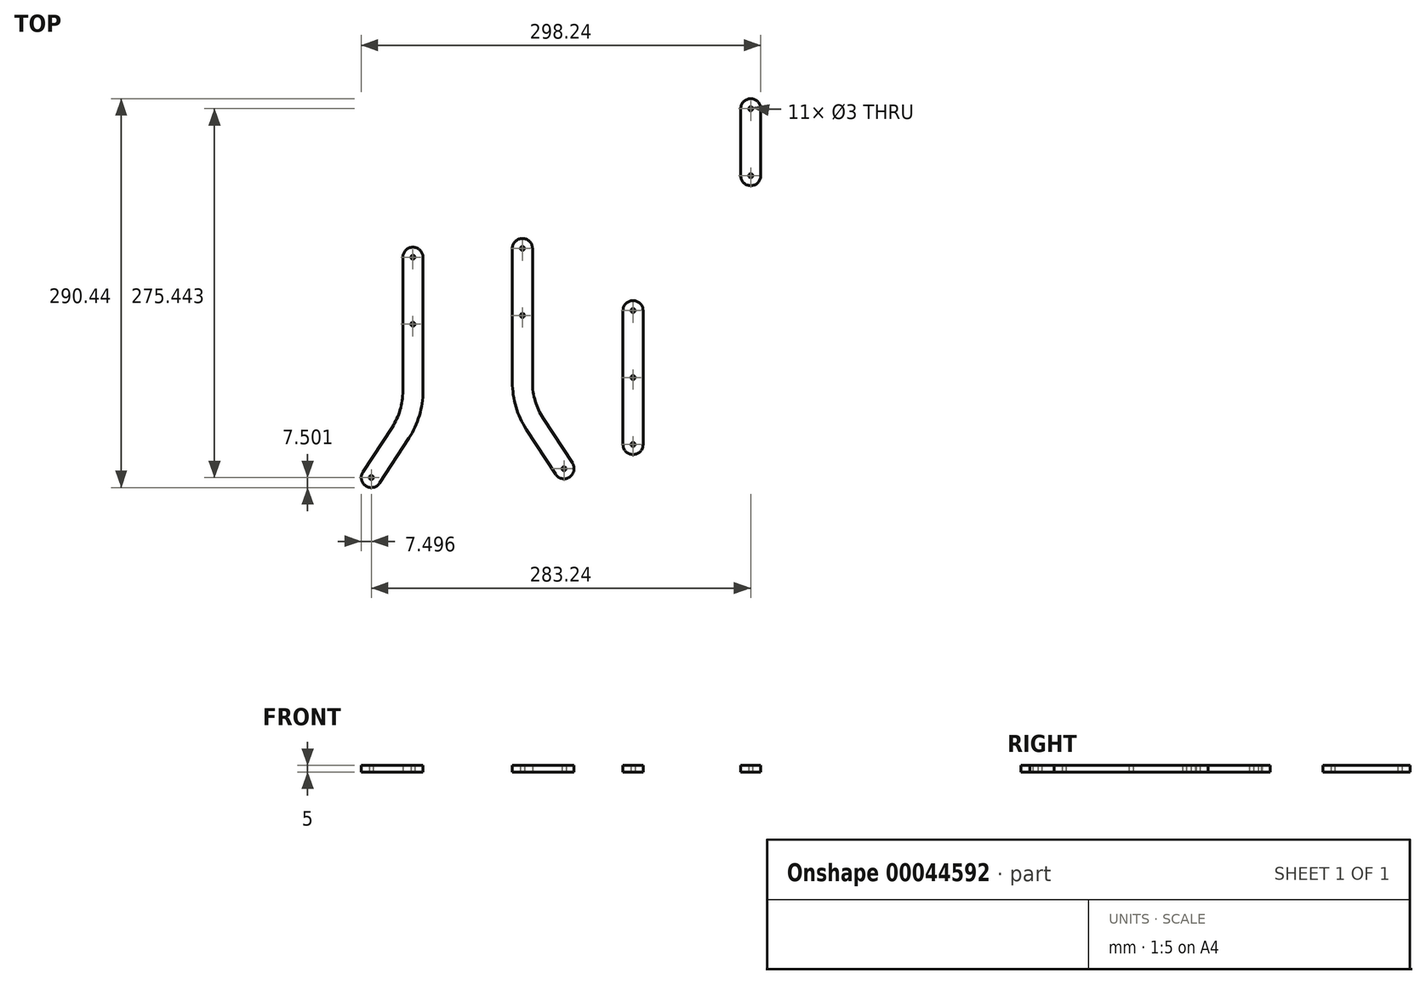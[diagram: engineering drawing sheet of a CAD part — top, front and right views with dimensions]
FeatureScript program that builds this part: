
annotation { "Feature Type Name" : "Feature", "Feature Type Description" : "" }
export const myFeature = defineFeature(function(context is Context, id is Id, definition is map)
    precondition{}
    {
        {
            var Q0;
            Q0=qCreatedBy(makeId("Top.planeOp"),FACE);
            var sketch = newSketch(context, id + "F0", { "sketchPlane" : qUnion([Q0])});
            skLineSegment(sketch, "E0", {"start": v(25.87, 19.2) * mm, "end": v(25.87, -80.8) * mm});
            skArc(sketch, "E1", {"start": v(25.87, -80.8) * mm, "mid": v(33.37, -88.3) * mm, "end": v(40.87, -80.8) * mm});
            skLineSegment(sketch, "E2", {"start": v(25.87, 19.2) * mm, "end": v(40.87, 19.2) * mm});
            skLineSegment(sketch, "E3", {"start": v(25.87, -80.8) * mm, "end": v(40.87, -80.8) * mm});
            skLineSegment(sketch, "E4", {"start": v(40.87, 19.2) * mm, "end": v(40.87, -80.8) * mm});
            skArc(sketch, "E5", {"start": v(40.87, 19.2) * mm, "mid": v(33.37, 26.7) * mm, "end": v(25.87, 19.2) * mm});
            skPoint(sketch, "E6", {"position": v(33.37, -30.8) * mm});
            skCircle(sketch, "E7", {"center": v(33.37, 19.2) * mm, "radius": 1.5 * mm});
            skCircle(sketch, "E8", {"center": v(33.37, -80.8) * mm, "radius": 1.5 * mm});
            skPoint(sketch, "E9", {"position": v(33.37, -5.8) * mm});
            skCircle(sketch, "E10", {"center": v(33.37, -30.8) * mm, "radius": 1.5 * mm});
            skSolve(sketch);
        }
        {
            var Q0;
            {var subQ9=sQuery(id+"F0.wireOp",EDGE,"E0");Q0=makeQuery(id+"F0.imprint","IMPRINT",FACE,{"disambiguationData":[TD([[makeQuery(id+"F0.imprint","IMPRINT",EDGE,{"derivedFrom":subQ9}),1.0]])]});}
            var Q1;
            {var subQ4=sQuery(id+"F0.wireOp",EDGE,"E5");Q1=makeQuery(id+"F0.imprint","IMPRINT",FACE,{"disambiguationData":[TD([[makeQuery(id+"F0.imprint","IMPRINT",EDGE,{"derivedFrom":subQ4}),1.0]])]});}
            var Q2;
            {var subQ4=sQuery(id+"F0.wireOp",EDGE,"E1");Q2=makeQuery(id+"F0.imprint","IMPRINT",FACE,{"disambiguationData":[TD([[makeQuery(id+"F0.imprint","IMPRINT",EDGE,{"derivedFrom":subQ4}),1.0]])]});}
            extrude(context, id + "F1", {"entities" : qUnion([Q0, Q1, Q2]), "depth" : 5 * mm});
        }
        {
            var Q0;
            Q0=qCreatedBy(makeId("Top.planeOp"),FACE);
            var sketch = newSketch(context, id + "F2", { "sketchPlane" : qUnion([Q0])});
            skLineSegment(sketch, "E11", {"start": v(-56.7, 65.62) * mm, "end": v(-56.7, -34.38) * mm});
            skArc(sketch, "E12", {"start": v(-56.7, -34.38) * mm, "mid": v(-54.04, -52.7) * mm, "end": v(-46.27, -69.49) * mm});
            skLineSegment(sketch, "E13", {"start": v(-46.27, -69.49) * mm, "end": v(-24.43, -103) * mm});
            skLineSegment(sketch, "E14", {"start": v(-24.43, -103) * mm, "end": v(-11.86, -94.8) * mm});
            skArc(sketch, "E15", {"start": v(-24.43, -103) * mm, "mid": v(-14.05, -105.19) * mm, "end": v(-11.86, -94.8) * mm});
            skLineSegment(sketch, "E16", {"start": v(-46.27, -69.49) * mm, "end": v(-33.7, -61.3) * mm});
            skLineSegment(sketch, "E17", {"start": v(-33.7, -61.3) * mm, "end": v(-11.86, -94.8) * mm});
            skLineSegment(sketch, "E18", {"start": v(-56.7, 65.62) * mm, "end": v(-41.7, 65.62) * mm});
            skLineSegment(sketch, "E19", {"start": v(-56.7, -34.38) * mm, "end": v(-41.7, -34.38) * mm});
            skLineSegment(sketch, "E20", {"start": v(-41.7, 65.62) * mm, "end": v(-41.7, -34.38) * mm});
            skArc(sketch, "E21", {"start": v(-41.7, -34.38) * mm, "mid": v(-39.66, -48.42) * mm, "end": v(-33.7, -61.3) * mm});
            skArc(sketch, "E22", {"start": v(-41.7, 65.62) * mm, "mid": v(-49.2, 73.12) * mm, "end": v(-56.7, 65.62) * mm});
            skLineSegment(sketch, "E23", {"start": v(-123.46, 59.06) * mm, "end": v(-123.46, -40.94) * mm});
            skLineSegment(sketch, "E24", {"start": v(-123.46, 59.06) * mm, "end": v(-138.46, 59.06) * mm});
            skArc(sketch, "E25", {"start": v(-123.46, 59.06) * mm, "mid": v(-130.96, 66.56) * mm, "end": v(-138.46, 59.06) * mm});
            skLineSegment(sketch, "E26", {"start": v(-138.46, 59.06) * mm, "end": v(-138.46, -40.94) * mm});
            skLineSegment(sketch, "E27", {"start": v(-138.46, -40.94) * mm, "end": v(-123.46, -40.94) * mm});
            skArc(sketch, "E28", {"start": v(-123.46, -40.94) * mm, "mid": v(-126.12, -59.26) * mm, "end": v(-133.9, -76.05) * mm});
            skLineSegment(sketch, "E29", {"start": v(-133.9, -76.05) * mm, "end": v(-155.73, -109.56) * mm});
            skLineSegment(sketch, "E30", {"start": v(-155.73, -109.56) * mm, "end": v(-168.3, -101.37) * mm});
            skLineSegment(sketch, "E31", {"start": v(-133.9, -76.05) * mm, "end": v(-146.46, -67.86) * mm});
            skLineSegment(sketch, "E32", {"start": v(-146.46, -67.86) * mm, "end": v(-168.3, -101.37) * mm});
            skArc(sketch, "E33", {"start": v(-146.46, -67.86) * mm, "mid": v(-140.5, -54.98) * mm, "end": v(-138.46, -40.94) * mm});
            skArc(sketch, "E34", {"start": v(-168.3, -101.37) * mm, "mid": v(-166.1, -111.75) * mm, "end": v(-155.73, -109.56) * mm});
            skPoint(sketch, "E35", {"position": v(-111.62, 71.38) * mm});
            skCircle(sketch, "E36", {"center": v(-130.96, 59.06) * mm, "radius": 1.5 * mm});
            skCircle(sketch, "E37", {"center": v(-162.01, -105.47) * mm, "radius": 1.5 * mm});
            skLineSegment(sketch, "E38", {"start": v(-130.96, 59.06) * mm, "end": v(-130.96, 9.06) * mm});
            skCircle(sketch, "E39", {"center": v(-130.96, 9.06) * mm, "radius": 1.5 * mm});
            skCircle(sketch, "E40", {"center": v(-49.2, 65.62) * mm, "radius": 1.5 * mm});
            skLineSegment(sketch, "E41", {"start": v(-49.2, 65.62) * mm, "end": v(-49.2, 15.62) * mm});
            skCircle(sketch, "E42", {"center": v(-49.2, 15.62) * mm, "radius": 1.5 * mm});
            skCircle(sketch, "E43", {"center": v(-18.14, -98.9) * mm, "radius": 1.5 * mm});
            skSolve(sketch);
        }
        {
            var Q0;
            {var subQ3=sQuery(id+"F2.wireOp",EDGE,"E22");Q0=makeQuery(id+"F2.imprint","IMPRINT",FACE,{"disambiguationData":[TD([[makeQuery(id+"F2.imprint","IMPRINT",EDGE,{"derivedFrom":subQ3}),1.0]])]});}
            var Q1;
            {var subQ5=sQuery(id+"F2.wireOp",EDGE,"E11");Q1=makeQuery(id+"F2.imprint","IMPRINT",FACE,{"disambiguationData":[TD([[makeQuery(id+"F2.imprint","IMPRINT",EDGE,{"derivedFrom":subQ5}),1.0]])]});}
            var Q2;
            Q2=makeQuery(id+"F2.imprint","IMPRINT",FACE,{"disambiguationData":[TD([[makeQuery(id+"F2.imprint","IMPRINT",EDGE,{"derivedFrom":sQuery(id+"F2.wireOp",EDGE,"E12")}),1.0]])]});
            var Q3;
            {var subQ5=sQuery(id+"F2.wireOp",EDGE,"E13");Q3=makeQuery(id+"F2.imprint","IMPRINT",FACE,{"disambiguationData":[TD([[makeQuery(id+"F2.imprint","IMPRINT",EDGE,{"derivedFrom":subQ5}),1.0]])]});}
            var Q4;
            {var subQ4=sQuery(id+"F2.wireOp",EDGE,"E15");Q4=makeQuery(id+"F2.imprint","IMPRINT",FACE,{"disambiguationData":[TD([[makeQuery(id+"F2.imprint","IMPRINT",EDGE,{"derivedFrom":subQ4}),1.0]])]});}
            extrude(context, id + "F3", {"entities" : qUnion([Q0, Q1, Q2, Q3, Q4]), "depth" : 5 * mm});
        }
        {
            var Q0;
            {var subQ4=sQuery(id+"F2.wireOp",EDGE,"E25");Q0=makeQuery(id+"F2.imprint","IMPRINT",FACE,{"disambiguationData":[TD([[makeQuery(id+"F2.imprint","IMPRINT",EDGE,{"derivedFrom":subQ4}),1.0]])]});}
            var Q1;
            {var subQ0=sQuery(id+"F2.wireOp",EDGE,"E23");Q1=makeQuery(id+"F2.imprint","IMPRINT",FACE,{"disambiguationData":[TD([[makeQuery(id+"F2.imprint","IMPRINT",EDGE,{"derivedFrom":subQ0}),-1.0]])]});}
            var Q2;
            Q2=makeQuery(id+"F2.imprint","IMPRINT",FACE,{"disambiguationData":[TD([[makeQuery(id+"F2.imprint","IMPRINT",EDGE,{"derivedFrom":sQuery(id+"F2.wireOp",EDGE,"E27")}),-1.0]])]});
            var Q3;
            {var subQ5=sQuery(id+"F2.wireOp",EDGE,"E29");Q3=makeQuery(id+"F2.imprint","IMPRINT",FACE,{"disambiguationData":[TD([[makeQuery(id+"F2.imprint","IMPRINT",EDGE,{"derivedFrom":subQ5}),-1.0]])]});}
            var Q4;
            {var subQ4=sQuery(id+"F2.wireOp",EDGE,"E34");Q4=makeQuery(id+"F2.imprint","IMPRINT",FACE,{"disambiguationData":[TD([[makeQuery(id+"F2.imprint","IMPRINT",EDGE,{"derivedFrom":subQ4}),1.0]])]});}
            extrude(context, id + "F4", {"entities" : qUnion([Q0, Q1, Q2, Q3, Q4]), "depth" : 5 * mm});
        }
        {
            var Q0;
            Q0=qCreatedBy(makeId("Top.planeOp"),FACE);
            var sketch = newSketch(context, id + "F5", { "sketchPlane" : qUnion([Q0])});
            skLineSegment(sketch, "E44", {"start": v(113.73, 169.97) * mm, "end": v(113.73, 119.97) * mm});
            skLineSegment(sketch, "E45", {"start": v(113.73, 169.97) * mm, "end": v(128.73, 169.97) * mm});
            skLineSegment(sketch, "E46", {"start": v(128.73, 169.97) * mm, "end": v(128.73, 119.97) * mm});
            skLineSegment(sketch, "E47", {"start": v(113.73, 119.97) * mm, "end": v(128.73, 119.97) * mm});
            skArc(sketch, "E48", {"start": v(113.73, 119.97) * mm, "mid": v(121.23, 112.47) * mm, "end": v(128.73, 119.97) * mm});
            skArc(sketch, "E49", {"start": v(128.73, 169.97) * mm, "mid": v(121.23, 177.47) * mm, "end": v(113.73, 169.97) * mm});
            skCircle(sketch, "E50", {"center": v(121.23, 169.97) * mm, "radius": 1.5 * mm});
            skCircle(sketch, "E51", {"center": v(121.23, 119.97) * mm, "radius": 1.5 * mm});
            skSolve(sketch);
        }
        {
            var Q0;
            {var subQ4=sQuery(id+"F5.wireOp",EDGE,"E49");Q0=makeQuery(id+"F5.imprint","IMPRINT",FACE,{"disambiguationData":[TD([[makeQuery(id+"F5.imprint","IMPRINT",EDGE,{"derivedFrom":subQ4}),1.0]])]});}
            var Q1;
            {var subQ10=sQuery(id+"F5.wireOp",EDGE,"E44");Q1=makeQuery(id+"F5.imprint","IMPRINT",FACE,{"disambiguationData":[TD([[makeQuery(id+"F5.imprint","IMPRINT",EDGE,{"derivedFrom":subQ10}),1.0]])]});}
            var Q2;
            {var subQ4=sQuery(id+"F5.wireOp",EDGE,"E48");Q2=makeQuery(id+"F5.imprint","IMPRINT",FACE,{"disambiguationData":[TD([[makeQuery(id+"F5.imprint","IMPRINT",EDGE,{"derivedFrom":subQ4}),1.0]])]});}
            extrude(context, id + "F6", {"entities" : qUnion([Q0, Q1, Q2]), "depth" : 5 * mm});
        }
    });
